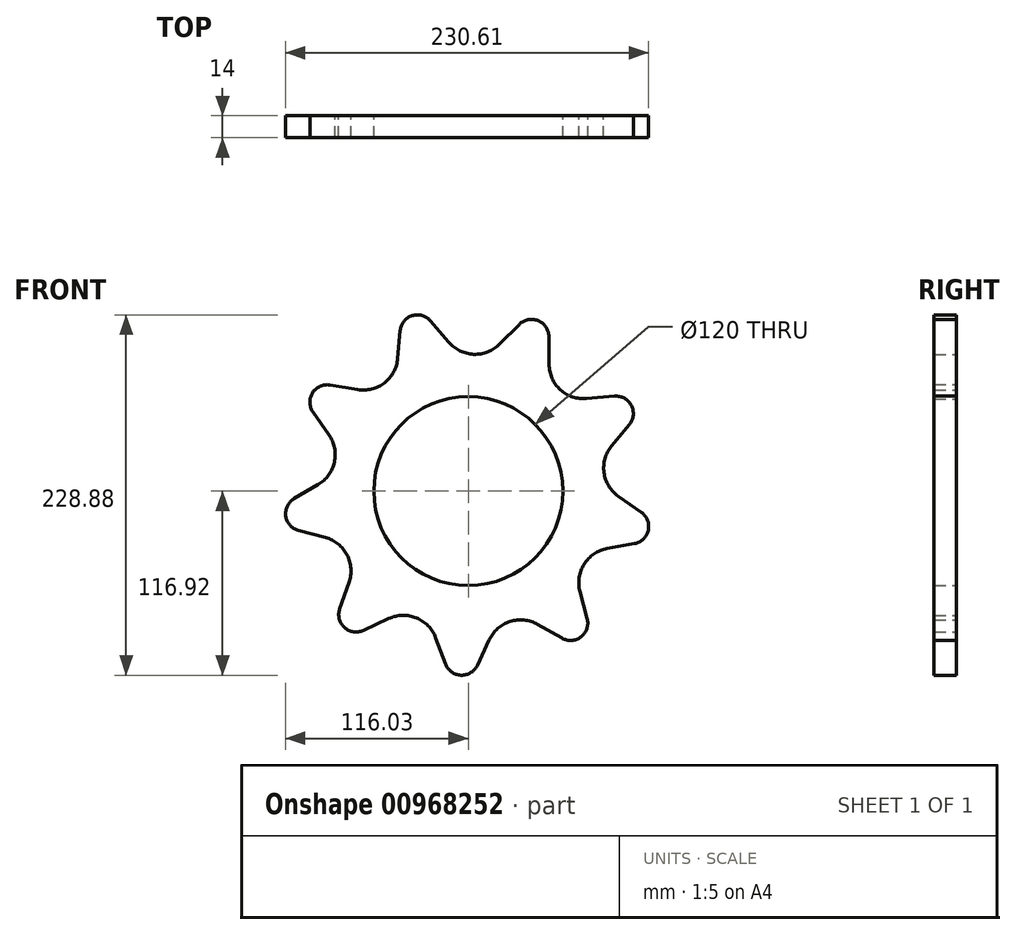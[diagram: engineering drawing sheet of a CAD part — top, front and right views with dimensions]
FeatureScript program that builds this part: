
annotation { "Feature Type Name" : "Feature", "Feature Type Description" : "" }
export const myFeature = defineFeature(function(context is Context, id is Id, definition is map)
    precondition{}
    {
        {
            var Q0;
            Q0=qCreatedBy(makeId("Front.planeOp"),FACE);
            var sketch = newSketch(context, id + "F0", { "sketchPlane" : qUnion([Q0])});
            skCircle(sketch, "E0", {"center": v(0, 0) * mm, "radius": 87 * mm});
            skCircle(sketch, "E1", {"center": v(-32.3, 100.96) * mm, "radius": 11 * mm});
            skCircle(sketch, "E2", {"center": v(40.15, 98.1) * mm, "radius": 11 * mm});
            skCircle(sketch, "E3", {"center": v(93.82, 49.34) * mm, "radius": 11 * mm});
            skCircle(sketch, "E4", {"center": v(103.58, -22.5) * mm, "radius": 11 * mm});
            skCircle(sketch, "E5", {"center": v(64.88, -83.82) * mm, "radius": 11 * mm});
            skCircle(sketch, "E6", {"center": v(-4.18, -105.92) * mm, "radius": 11 * mm});
            skCircle(sketch, "E7", {"center": v(-89.64, 56.58) * mm, "radius": 11 * mm});
            skCircle(sketch, "E8", {"center": v(-105.03, -14.28) * mm, "radius": 11 * mm});
            skCircle(sketch, "E9", {"center": v(-71.28, -78.45) * mm, "radius": 11 * mm});
            skLineSegment(sketch, "E10", {"start": v(0, 0) * mm, "end": v(-71.28, -78.45) * mm});
            skLineSegment(sketch, "E11", {"start": v(0, 0) * mm, "end": v(-4.18, -105.92) * mm});
            skLineSegment(sketch, "E12", {"start": v(0, 0) * mm, "end": v(64.88, -83.82) * mm});
            skLineSegment(sketch, "E13", {"start": v(0, 0) * mm, "end": v(103.58, -22.5) * mm});
            skLineSegment(sketch, "E14", {"start": v(0, 0) * mm, "end": v(93.82, 49.34) * mm});
            skLineSegment(sketch, "E15", {"start": v(0, 0) * mm, "end": v(40.15, 98.1) * mm});
            skLineSegment(sketch, "E16", {"start": v(0, 0) * mm, "end": v(-32.3, 100.96) * mm});
            skLineSegment(sketch, "E17", {"start": v(0, 0) * mm, "end": v(-89.64, 56.58) * mm});
            skLineSegment(sketch, "E18", {"start": v(0, 0) * mm, "end": v(-105.03, -14.28) * mm});
            skCircle(sketch, "E19", {"center": v(4.3, 108.92) * mm, "radius": 22 * mm});
            skCircle(sketch, "E20", {"center": v(73.3, 80.67) * mm, "radius": 22 * mm});
            skCircle(sketch, "E21", {"center": v(108, 14.68) * mm, "radius": 22 * mm});
            skCircle(sketch, "E22", {"center": v(92.18, -58.18) * mm, "radius": 22 * mm});
            skCircle(sketch, "E23", {"center": v(-66.72, 86.2) * mm, "radius": 22 * mm});
            skCircle(sketch, "E24", {"center": v(-106.52, 23.14) * mm, "radius": 22 * mm});
            skCircle(sketch, "E25", {"center": v(-96.47, -50.74) * mm, "radius": 22 * mm});
            skCircle(sketch, "E26", {"center": v(-41.29, -100.88) * mm, "radius": 22 * mm});
            skCircle(sketch, "E27", {"center": v(33.22, -103.82) * mm, "radius": 22 * mm});
            skLineSegment(sketch, "E28", {"start": v(4.3, 108.92) * mm, "end": v(0, 0) * mm});
            skLineSegment(sketch, "E29", {"start": v(0, 0) * mm, "end": v(73.3, 80.67) * mm});
            skLineSegment(sketch, "E30", {"start": v(0, 0) * mm, "end": v(108, 14.68) * mm});
            skLineSegment(sketch, "E31", {"start": v(0, 0) * mm, "end": v(92.18, -58.18) * mm});
            skLineSegment(sketch, "E32", {"start": v(0, 0) * mm, "end": v(33.22, -103.82) * mm});
            skLineSegment(sketch, "E33", {"start": v(0, 0) * mm, "end": v(-41.29, -100.88) * mm});
            skLineSegment(sketch, "E34", {"start": v(0, 0) * mm, "end": v(-96.47, -50.74) * mm});
            skLineSegment(sketch, "E35", {"start": v(0, 0) * mm, "end": v(-106.52, 23.14) * mm});
            skLineSegment(sketch, "E36", {"start": v(0, 0) * mm, "end": v(-66.72, 86.2) * mm});
            skLineSegment(sketch, "E37", {"start": v(-43.26, 101.92) * mm, "end": v(-44.8, 84.28) * mm});
            skLineSegment(sketch, "E38", {"start": v(-23.94, 108.1) * mm, "end": v(-12.44, 94.63) * mm});
            skLineSegment(sketch, "E39", {"start": v(-87.82, 67.42) * mm, "end": v(-70.36, 64.5) * mm});
            skLineSegment(sketch, "E40", {"start": v(-98.65, 50.27) * mm, "end": v(-88.5, 35.76) * mm});
            skLineSegment(sketch, "E41", {"start": v(-110.61, -4.8) * mm, "end": v(-95.35, 4.18) * mm});
            skLineSegment(sketch, "E42", {"start": v(-107.88, -24.9) * mm, "end": v(-90.78, -29.49) * mm});
            skLineSegment(sketch, "E43", {"start": v(-81.65, -74.78) * mm, "end": v(-75.73, -58.09) * mm});
            skLineSegment(sketch, "E44", {"start": v(-66.63, -88.42) * mm, "end": v(-50.58, -80.94) * mm});
            skLineSegment(sketch, "E45", {"start": v(-14.48, -109.77) * mm, "end": v(-20.68, -93.18) * mm});
            skLineSegment(sketch, "E46", {"start": v(5.8, -110.57) * mm, "end": v(13.28, -94.52) * mm});
            skLineSegment(sketch, "E47", {"start": v(59.46, -93.4) * mm, "end": v(44.05, -84.67) * mm});
            skLineSegment(sketch, "E48", {"start": v(75.5, -80.98) * mm, "end": v(70.93, -63.87) * mm});
            skLineSegment(sketch, "E49", {"start": v(105.59, -33.32) * mm, "end": v(88.17, -36.54) * mm});
            skLineSegment(sketch, "E50", {"start": v(109.9, -13.5) * mm, "end": v(95.39, -3.34) * mm});
            skLineSegment(sketch, "E51", {"start": v(102.3, 42.34) * mm, "end": v(91.03, 28.68) * mm});
            skLineSegment(sketch, "E52", {"start": v(92.86, 60.3) * mm, "end": v(75.22, 58.76) * mm});
            skLineSegment(sketch, "E53", {"start": v(51.15, 98.2) * mm, "end": v(51.3, 80.49) * mm});
            skLineSegment(sketch, "E54", {"start": v(32.37, 105.88) * mm, "end": v(19.85, 93.36) * mm});
            skCircle(sketch, "E55", {"center": v(0, 0) * mm, "radius": 60 * mm});
            skSolve(sketch);
        }
        {
            var Q0;
            {var subQ0=sQuery(id+"F0.wireOp",EDGE,"E2");var subQ1=makeQuery(id+"F0.imprint","INTERSECT",VERTEX,{"derivedFrom":[subQ0,sQuery(id+"F0.wireOp",EDGE,"E53")]});Q0=makeQuery(id+"F0.imprint","IMPRINT",FACE,{"disambiguationData":[TD([[makeQuery(id+"F0.imprint","IMPRINT",EDGE,{"disambiguationData":[TD([[subQ1,-1.0]])],"derivedFrom":subQ0}),1.0]])]});}
            var Q1;
            {var subQ0=sQuery(id+"F0.wireOp",EDGE,"E53");Q1=makeQuery(id+"F0.imprint","IMPRINT",FACE,{"disambiguationData":[TD([[makeQuery(id+"F0.imprint","IMPRINT",EDGE,{"derivedFrom":subQ0}),-1.0]])]});}
            var Q2;
            {var subQ0=sQuery(id+"F0.wireOp",EDGE,"E54");Q2=makeQuery(id+"F0.imprint","IMPRINT",FACE,{"disambiguationData":[TD([[makeQuery(id+"F0.imprint","IMPRINT",EDGE,{"derivedFrom":subQ0}),1.0]])]});}
            var Q3;
            {var subQ0=sQuery(id+"F0.wireOp",EDGE,"E15");var subQ1=sQuery(id+"F0.wireOp",EDGE,"E0");var subQ2=makeQuery(id+"F0.imprint","INTERSECT",VERTEX,{"derivedFrom":[subQ1,subQ0]});Q3=makeQuery(id+"F0.imprint","IMPRINT",FACE,{"disambiguationData":[TD([[makeQuery(id+"F0.imprint","IMPRINT",EDGE,{"disambiguationData":[TD([[subQ2,-1.0]])],"derivedFrom":subQ1}),1.0]])]});}
            var Q4;
            {var subQ0=sQuery(id+"F0.wireOp",EDGE,"E15");var subQ1=sQuery(id+"F0.wireOp",EDGE,"E0");var subQ2=makeQuery(id+"F0.imprint","INTERSECT",VERTEX,{"derivedFrom":[subQ1,subQ0]});Q4=makeQuery(id+"F0.imprint","IMPRINT",FACE,{"disambiguationData":[TD([[makeQuery(id+"F0.imprint","IMPRINT",EDGE,{"disambiguationData":[TD([[subQ2,1.0]])],"derivedFrom":subQ1}),1.0]])]});}
            var Q5;
            {var subQ0=sQuery(id+"F0.wireOp",EDGE,"E52");Q5=makeQuery(id+"F0.imprint","IMPRINT",FACE,{"disambiguationData":[TD([[makeQuery(id+"F0.imprint","IMPRINT",EDGE,{"derivedFrom":subQ0}),1.0]])]});}
            var Q6;
            {var subQ0=sQuery(id+"F0.wireOp",EDGE,"E3");var subQ1=makeQuery(id+"F0.imprint","INTERSECT",VERTEX,{"derivedFrom":[subQ0,sQuery(id+"F0.wireOp",EDGE,"E52")]});Q6=makeQuery(id+"F0.imprint","IMPRINT",FACE,{"disambiguationData":[TD([[makeQuery(id+"F0.imprint","IMPRINT",EDGE,{"disambiguationData":[TD([[subQ1,-1.0]])],"derivedFrom":subQ0}),1.0]])]});}
            var Q7;
            {var subQ0=sQuery(id+"F0.wireOp",EDGE,"E51");Q7=makeQuery(id+"F0.imprint","IMPRINT",FACE,{"disambiguationData":[TD([[makeQuery(id+"F0.imprint","IMPRINT",EDGE,{"derivedFrom":subQ0}),-1.0]])]});}
            var Q8;
            {var subQ0=sQuery(id+"F0.wireOp",EDGE,"E14");var subQ1=sQuery(id+"F0.wireOp",EDGE,"E0");var subQ2=makeQuery(id+"F0.imprint","INTERSECT",VERTEX,{"derivedFrom":[subQ1,subQ0]});Q8=makeQuery(id+"F0.imprint","IMPRINT",FACE,{"disambiguationData":[TD([[makeQuery(id+"F0.imprint","IMPRINT",EDGE,{"disambiguationData":[TD([[subQ2,-1.0]])],"derivedFrom":subQ1}),1.0]])]});}
            var Q9;
            {var subQ0=sQuery(id+"F0.wireOp",EDGE,"E14");var subQ1=sQuery(id+"F0.wireOp",EDGE,"E0");var subQ2=makeQuery(id+"F0.imprint","INTERSECT",VERTEX,{"derivedFrom":[subQ1,subQ0]});Q9=makeQuery(id+"F0.imprint","IMPRINT",FACE,{"disambiguationData":[TD([[makeQuery(id+"F0.imprint","IMPRINT",EDGE,{"disambiguationData":[TD([[subQ2,1.0]])],"derivedFrom":subQ1}),1.0]])]});}
            var Q10;
            {var subQ0=sQuery(id+"F0.wireOp",EDGE,"E13");var subQ1=sQuery(id+"F0.wireOp",EDGE,"E0");var subQ2=makeQuery(id+"F0.imprint","INTERSECT",VERTEX,{"derivedFrom":[subQ1,subQ0]});Q10=makeQuery(id+"F0.imprint","IMPRINT",FACE,{"disambiguationData":[TD([[makeQuery(id+"F0.imprint","IMPRINT",EDGE,{"disambiguationData":[TD([[subQ2,-1.0]])],"derivedFrom":subQ1}),1.0]])]});}
            var Q11;
            {var subQ0=sQuery(id+"F0.wireOp",EDGE,"E50");Q11=makeQuery(id+"F0.imprint","IMPRINT",FACE,{"disambiguationData":[TD([[makeQuery(id+"F0.imprint","IMPRINT",EDGE,{"derivedFrom":subQ0}),1.0]])]});}
            var Q12;
            {var subQ0=sQuery(id+"F0.wireOp",EDGE,"E4");var subQ1=makeQuery(id+"F0.imprint","INTERSECT",VERTEX,{"derivedFrom":[subQ0,sQuery(id+"F0.wireOp",EDGE,"E50")]});Q12=makeQuery(id+"F0.imprint","IMPRINT",FACE,{"disambiguationData":[TD([[makeQuery(id+"F0.imprint","IMPRINT",EDGE,{"disambiguationData":[TD([[subQ1,-1.0]])],"derivedFrom":subQ0}),1.0]])]});}
            var Q13;
            {var subQ0=sQuery(id+"F0.wireOp",EDGE,"E49");Q13=makeQuery(id+"F0.imprint","IMPRINT",FACE,{"disambiguationData":[TD([[makeQuery(id+"F0.imprint","IMPRINT",EDGE,{"derivedFrom":subQ0}),-1.0]])]});}
            var Q14;
            {var subQ0=sQuery(id+"F0.wireOp",EDGE,"E13");var subQ1=sQuery(id+"F0.wireOp",EDGE,"E0");var subQ2=makeQuery(id+"F0.imprint","INTERSECT",VERTEX,{"derivedFrom":[subQ1,subQ0]});Q14=makeQuery(id+"F0.imprint","IMPRINT",FACE,{"disambiguationData":[TD([[makeQuery(id+"F0.imprint","IMPRINT",EDGE,{"disambiguationData":[TD([[subQ2,1.0]])],"derivedFrom":subQ1}),1.0]])]});}
            var Q15;
            {var subQ0=sQuery(id+"F0.wireOp",EDGE,"E12");var subQ1=sQuery(id+"F0.wireOp",EDGE,"E0");var subQ2=makeQuery(id+"F0.imprint","INTERSECT",VERTEX,{"derivedFrom":[subQ1,subQ0]});Q15=makeQuery(id+"F0.imprint","IMPRINT",FACE,{"disambiguationData":[TD([[makeQuery(id+"F0.imprint","IMPRINT",EDGE,{"disambiguationData":[TD([[subQ2,-1.0]])],"derivedFrom":subQ1}),1.0]])]});}
            var Q16;
            {var subQ0=sQuery(id+"F0.wireOp",EDGE,"E48");Q16=makeQuery(id+"F0.imprint","IMPRINT",FACE,{"disambiguationData":[TD([[makeQuery(id+"F0.imprint","IMPRINT",EDGE,{"derivedFrom":subQ0}),1.0]])]});}
            var Q17;
            {var subQ0=sQuery(id+"F0.wireOp",EDGE,"E5");var subQ1=makeQuery(id+"F0.imprint","INTERSECT",VERTEX,{"derivedFrom":[subQ0,sQuery(id+"F0.wireOp",EDGE,"E48")]});Q17=makeQuery(id+"F0.imprint","IMPRINT",FACE,{"disambiguationData":[TD([[makeQuery(id+"F0.imprint","IMPRINT",EDGE,{"disambiguationData":[TD([[subQ1,-1.0]])],"derivedFrom":subQ0}),1.0]])]});}
            var Q18;
            {var subQ0=sQuery(id+"F0.wireOp",EDGE,"E47");Q18=makeQuery(id+"F0.imprint","IMPRINT",FACE,{"disambiguationData":[TD([[makeQuery(id+"F0.imprint","IMPRINT",EDGE,{"derivedFrom":subQ0}),-1.0]])]});}
            var Q19;
            {var subQ0=sQuery(id+"F0.wireOp",EDGE,"E12");var subQ1=sQuery(id+"F0.wireOp",EDGE,"E0");var subQ2=makeQuery(id+"F0.imprint","INTERSECT",VERTEX,{"derivedFrom":[subQ1,subQ0]});Q19=makeQuery(id+"F0.imprint","IMPRINT",FACE,{"disambiguationData":[TD([[makeQuery(id+"F0.imprint","IMPRINT",EDGE,{"disambiguationData":[TD([[subQ2,1.0]])],"derivedFrom":subQ1}),1.0]])]});}
            var Q20;
            {var subQ0=sQuery(id+"F0.wireOp",EDGE,"E11");var subQ1=sQuery(id+"F0.wireOp",EDGE,"E0");var subQ2=makeQuery(id+"F0.imprint","INTERSECT",VERTEX,{"derivedFrom":[subQ1,subQ0]});Q20=makeQuery(id+"F0.imprint","IMPRINT",FACE,{"disambiguationData":[TD([[makeQuery(id+"F0.imprint","IMPRINT",EDGE,{"disambiguationData":[TD([[subQ2,-1.0]])],"derivedFrom":subQ1}),1.0]])]});}
            var Q21;
            {var subQ0=sQuery(id+"F0.wireOp",EDGE,"E6");var subQ1=makeQuery(id+"F0.imprint","INTERSECT",VERTEX,{"derivedFrom":[subQ0,sQuery(id+"F0.wireOp",EDGE,"E45")]});Q21=makeQuery(id+"F0.imprint","IMPRINT",FACE,{"disambiguationData":[TD([[makeQuery(id+"F0.imprint","IMPRINT",EDGE,{"disambiguationData":[TD([[subQ1,1.0]])],"derivedFrom":subQ0}),1.0]])]});}
            var Q22;
            {var subQ0=sQuery(id+"F0.wireOp",EDGE,"E46");Q22=makeQuery(id+"F0.imprint","IMPRINT",FACE,{"disambiguationData":[TD([[makeQuery(id+"F0.imprint","IMPRINT",EDGE,{"derivedFrom":subQ0}),1.0]])]});}
            var Q23;
            {var subQ0=sQuery(id+"F0.wireOp",EDGE,"E45");Q23=makeQuery(id+"F0.imprint","IMPRINT",FACE,{"disambiguationData":[TD([[makeQuery(id+"F0.imprint","IMPRINT",EDGE,{"derivedFrom":subQ0}),-1.0]])]});}
            var Q24;
            {var subQ0=sQuery(id+"F0.wireOp",EDGE,"E44");Q24=makeQuery(id+"F0.imprint","IMPRINT",FACE,{"disambiguationData":[TD([[makeQuery(id+"F0.imprint","IMPRINT",EDGE,{"derivedFrom":subQ0}),1.0]])]});}
            var Q25;
            {var subQ0=sQuery(id+"F0.wireOp",EDGE,"E9");var subQ1=makeQuery(id+"F0.imprint","INTERSECT",VERTEX,{"derivedFrom":[subQ0,sQuery(id+"F0.wireOp",EDGE,"E43")]});Q25=makeQuery(id+"F0.imprint","IMPRINT",FACE,{"disambiguationData":[TD([[makeQuery(id+"F0.imprint","IMPRINT",EDGE,{"disambiguationData":[TD([[subQ1,1.0]])],"derivedFrom":subQ0}),1.0]])]});}
            var Q26;
            {var subQ0=sQuery(id+"F0.wireOp",EDGE,"E43");Q26=makeQuery(id+"F0.imprint","IMPRINT",FACE,{"disambiguationData":[TD([[makeQuery(id+"F0.imprint","IMPRINT",EDGE,{"derivedFrom":subQ0}),-1.0]])]});}
            var Q27;
            {var subQ5=sQuery(id+"F0.wireOp",EDGE,"E42");Q27=makeQuery(id+"F0.imprint","IMPRINT",FACE,{"disambiguationData":[TD([[makeQuery(id+"F0.imprint","IMPRINT",EDGE,{"derivedFrom":subQ5}),1.0]])]});}
            var Q28;
            {var subQ0=sQuery(id+"F0.wireOp",EDGE,"E8");var subQ1=makeQuery(id+"F0.imprint","INTERSECT",VERTEX,{"derivedFrom":[subQ0,sQuery(id+"F0.wireOp",EDGE,"E41")]});Q28=makeQuery(id+"F0.imprint","IMPRINT",FACE,{"disambiguationData":[TD([[makeQuery(id+"F0.imprint","IMPRINT",EDGE,{"disambiguationData":[TD([[subQ1,1.0]])],"derivedFrom":subQ0}),1.0]])]});}
            var Q29;
            {var subQ5=sQuery(id+"F0.wireOp",EDGE,"E41");Q29=makeQuery(id+"F0.imprint","IMPRINT",FACE,{"disambiguationData":[TD([[makeQuery(id+"F0.imprint","IMPRINT",EDGE,{"derivedFrom":subQ5}),-1.0]])]});}
            var Q30;
            {var subQ0=sQuery(id+"F0.wireOp",EDGE,"E7");var subQ1=makeQuery(id+"F0.imprint","INTERSECT",VERTEX,{"derivedFrom":[subQ0,sQuery(id+"F0.wireOp",EDGE,"E39")]});Q30=makeQuery(id+"F0.imprint","IMPRINT",FACE,{"disambiguationData":[TD([[makeQuery(id+"F0.imprint","IMPRINT",EDGE,{"disambiguationData":[TD([[subQ1,-1.0]])],"derivedFrom":subQ0}),1.0]])]});}
            var Q31;
            {var subQ0=sQuery(id+"F0.wireOp",EDGE,"E40");Q31=makeQuery(id+"F0.imprint","IMPRINT",FACE,{"disambiguationData":[TD([[makeQuery(id+"F0.imprint","IMPRINT",EDGE,{"derivedFrom":subQ0}),1.0]])]});}
            var Q32;
            {var subQ0=sQuery(id+"F0.wireOp",EDGE,"E39");Q32=makeQuery(id+"F0.imprint","IMPRINT",FACE,{"disambiguationData":[TD([[makeQuery(id+"F0.imprint","IMPRINT",EDGE,{"derivedFrom":subQ0}),-1.0]])]});}
            var Q33;
            {var subQ0=sQuery(id+"F0.wireOp",EDGE,"E37");Q33=makeQuery(id+"F0.imprint","IMPRINT",FACE,{"disambiguationData":[TD([[makeQuery(id+"F0.imprint","IMPRINT",EDGE,{"derivedFrom":subQ0}),1.0]])]});}
            var Q34;
            {var subQ0=sQuery(id+"F0.wireOp",EDGE,"E38");Q34=makeQuery(id+"F0.imprint","IMPRINT",FACE,{"disambiguationData":[TD([[makeQuery(id+"F0.imprint","IMPRINT",EDGE,{"derivedFrom":subQ0}),-1.0]])]});}
            var Q35;
            {var subQ0=sQuery(id+"F0.wireOp",EDGE,"E1");var subQ1=makeQuery(id+"F0.imprint","INTERSECT",VERTEX,{"derivedFrom":[subQ0,sQuery(id+"F0.wireOp",EDGE,"E37")]});Q35=makeQuery(id+"F0.imprint","IMPRINT",FACE,{"disambiguationData":[TD([[makeQuery(id+"F0.imprint","IMPRINT",EDGE,{"disambiguationData":[TD([[subQ1,1.0]])],"derivedFrom":subQ0}),1.0]])]});}
            var Q36;
            {var subQ0=sQuery(id+"F0.wireOp",EDGE,"E16");var subQ1=sQuery(id+"F0.wireOp",EDGE,"E0");var subQ2=makeQuery(id+"F0.imprint","INTERSECT",VERTEX,{"derivedFrom":[subQ1,subQ0]});Q36=makeQuery(id+"F0.imprint","IMPRINT",FACE,{"disambiguationData":[TD([[makeQuery(id+"F0.imprint","IMPRINT",EDGE,{"disambiguationData":[TD([[subQ2,1.0]])],"derivedFrom":subQ1}),1.0]])]});}
            var Q37;
            {var subQ0=sQuery(id+"F0.wireOp",EDGE,"E16");var subQ1=sQuery(id+"F0.wireOp",EDGE,"E0");var subQ2=makeQuery(id+"F0.imprint","INTERSECT",VERTEX,{"derivedFrom":[subQ1,subQ0]});Q37=makeQuery(id+"F0.imprint","IMPRINT",FACE,{"disambiguationData":[TD([[makeQuery(id+"F0.imprint","IMPRINT",EDGE,{"disambiguationData":[TD([[subQ2,-1.0]])],"derivedFrom":subQ1}),1.0]])]});}
            var Q38;
            {var subQ0=sQuery(id+"F0.wireOp",EDGE,"E17");var subQ1=sQuery(id+"F0.wireOp",EDGE,"E0");var subQ2=makeQuery(id+"F0.imprint","INTERSECT",VERTEX,{"derivedFrom":[subQ1,subQ0]});Q38=makeQuery(id+"F0.imprint","IMPRINT",FACE,{"disambiguationData":[TD([[makeQuery(id+"F0.imprint","IMPRINT",EDGE,{"disambiguationData":[TD([[subQ2,1.0]])],"derivedFrom":subQ1}),1.0]])]});}
            var Q39;
            {var subQ0=sQuery(id+"F0.wireOp",EDGE,"E17");var subQ1=sQuery(id+"F0.wireOp",EDGE,"E0");var subQ2=makeQuery(id+"F0.imprint","INTERSECT",VERTEX,{"derivedFrom":[subQ1,subQ0]});Q39=makeQuery(id+"F0.imprint","IMPRINT",FACE,{"disambiguationData":[TD([[makeQuery(id+"F0.imprint","IMPRINT",EDGE,{"disambiguationData":[TD([[subQ2,-1.0]])],"derivedFrom":subQ1}),1.0]])]});}
            var Q40;
            {var subQ0=sQuery(id+"F0.wireOp",EDGE,"E18");var subQ1=sQuery(id+"F0.wireOp",EDGE,"E0");var subQ2=makeQuery(id+"F0.imprint","INTERSECT",VERTEX,{"derivedFrom":[subQ1,subQ0]});Q40=makeQuery(id+"F0.imprint","IMPRINT",FACE,{"disambiguationData":[TD([[makeQuery(id+"F0.imprint","IMPRINT",EDGE,{"disambiguationData":[TD([[subQ2,1.0]])],"derivedFrom":subQ1}),1.0]])]});}
            var Q41;
            {var subQ0=sQuery(id+"F0.wireOp",EDGE,"E18");var subQ1=sQuery(id+"F0.wireOp",EDGE,"E0");var subQ2=makeQuery(id+"F0.imprint","INTERSECT",VERTEX,{"derivedFrom":[subQ1,subQ0]});Q41=makeQuery(id+"F0.imprint","IMPRINT",FACE,{"disambiguationData":[TD([[makeQuery(id+"F0.imprint","IMPRINT",EDGE,{"disambiguationData":[TD([[subQ2,-1.0]])],"derivedFrom":subQ1}),1.0]])]});}
            var Q42;
            {var subQ0=sQuery(id+"F0.wireOp",EDGE,"E10");var subQ1=sQuery(id+"F0.wireOp",EDGE,"E0");var subQ2=makeQuery(id+"F0.imprint","INTERSECT",VERTEX,{"derivedFrom":[subQ1,subQ0]});Q42=makeQuery(id+"F0.imprint","IMPRINT",FACE,{"disambiguationData":[TD([[makeQuery(id+"F0.imprint","IMPRINT",EDGE,{"disambiguationData":[TD([[subQ2,1.0]])],"derivedFrom":subQ1}),1.0]])]});}
            var Q43;
            {var subQ0=sQuery(id+"F0.wireOp",EDGE,"E10");var subQ1=sQuery(id+"F0.wireOp",EDGE,"E0");var subQ2=makeQuery(id+"F0.imprint","INTERSECT",VERTEX,{"derivedFrom":[subQ1,subQ0]});Q43=makeQuery(id+"F0.imprint","IMPRINT",FACE,{"disambiguationData":[TD([[makeQuery(id+"F0.imprint","IMPRINT",EDGE,{"disambiguationData":[TD([[subQ2,-1.0]])],"derivedFrom":subQ1}),1.0]])]});}
            var Q44;
            {var subQ0=sQuery(id+"F0.wireOp",EDGE,"E11");var subQ1=sQuery(id+"F0.wireOp",EDGE,"E0");var subQ2=makeQuery(id+"F0.imprint","INTERSECT",VERTEX,{"derivedFrom":[subQ1,subQ0]});Q44=makeQuery(id+"F0.imprint","IMPRINT",FACE,{"disambiguationData":[TD([[makeQuery(id+"F0.imprint","IMPRINT",EDGE,{"disambiguationData":[TD([[subQ2,1.0]])],"derivedFrom":subQ1}),1.0]])]});}
            extrude(context, id + "F1", {"entities" : qUnion([Q0, Q1, Q2, Q3, Q4, Q5, Q6, Q7, Q8, Q9, Q10, Q11, Q12, Q13, Q14, Q15, Q16, Q17, Q18, Q19, Q20, Q21, Q22, Q23, Q24, Q25, Q26, Q27, Q28, Q29, Q30, Q31, Q32, Q33, Q34, Q35, Q36, Q37, Q38, Q39, Q40, Q41, Q42, Q43, Q44]), "depth" : 14 * mm, "offsetDistance" : 25 * mm});
        }
    });
